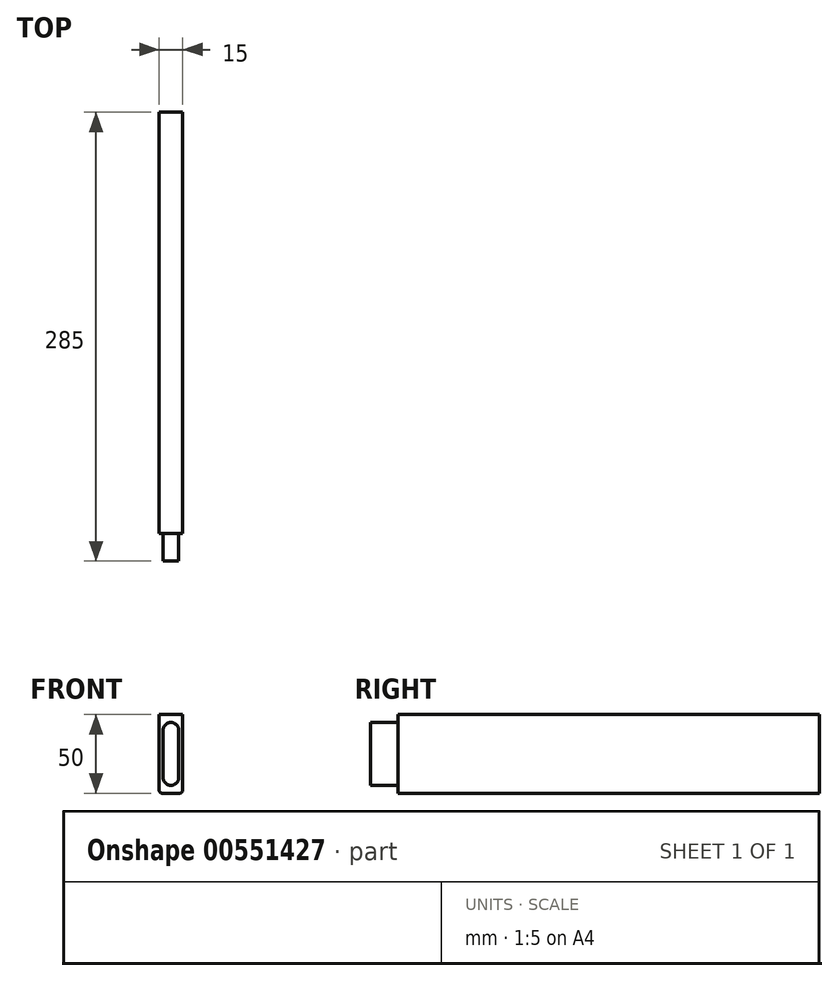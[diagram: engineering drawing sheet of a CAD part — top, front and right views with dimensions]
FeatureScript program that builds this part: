
annotation { "Feature Type Name" : "Feature", "Feature Type Description" : "" }
export const myFeature = defineFeature(function(context is Context, id is Id, definition is map)
    precondition{}
    {
        {
            var Q0;
            Q0=qCreatedBy(makeId("Front.planeOp"),FACE);
            var sketch = newSketch(context, id + "F0", { "sketchPlane" : qUnion([Q0])});
            skLineSegment(sketch, "E0.bottom", {"start": v(-7.5, -25) * mm, "end": v(7.5, -25) * mm});
            skLineSegment(sketch, "E0.top", {"start": v(-7.5, 25) * mm, "end": v(7.5, 25) * mm});
            skLineSegment(sketch, "E0.left", {"start": v(-7.5, -25) * mm, "end": v(-7.5, 25) * mm});
            skLineSegment(sketch, "E0.right", {"start": v(7.5, -25) * mm, "end": v(7.5, 25) * mm});
            skPoint(sketch, "E0.middle", {"position": v(0, 0) * mm});
            skSolve(sketch);
        }
        {
            var Q0;
            Q0 = qSketchRegion(id + "F0", true);
            extrude(context, id + "F1", {"entities" : qUnion([Q0]), "depth" : 142.5 * mm, "offsetDistance" : 25 * mm, "hasSecondDirection" : true, "secondDirectionOppositeDirection" : true, "secondDirectionDepth" : 142.5 * mm});
        }
        {
            var Q0;
            Q0=makeQuery(id+"F1.opExtrude","CAP_FACE",FACE,{"disambiguationData":[OSD([sQuery(id+"F0.wireOp",EDGE,"E0.bottom"),sQuery(id+"F0.wireOp",EDGE,"E0.top"),sQuery(id+"F0.wireOp",EDGE,"E0.left"),sQuery(id+"F0.wireOp",EDGE,"E0.right")])],"isStart":false});
            var sketch = newSketch(context, id + "F2", { "sketchPlane" : qUnion([Q0])});
            skLineSegment(sketch, "E1.bottom", {"start": v(-5, -15) * mm, "end": v(5, -15) * mm});
            skLineSegment(sketch, "E1.top", {"start": v(-5, 15) * mm, "end": v(5, 15) * mm});
            skLineSegment(sketch, "E1.left", {"start": v(-5, -15) * mm, "end": v(-5, 15) * mm});
            skLineSegment(sketch, "E1.right", {"start": v(5, -15) * mm, "end": v(5, 15) * mm});
            skPoint(sketch, "E1.middle", {"position": v(0, 0) * mm});
            skCircle(sketch, "E2", {"center": v(0, 15) * mm, "radius": 5 * mm});
            skCircle(sketch, "E3", {"center": v(0, -15) * mm, "radius": 5 * mm});
            skLineSegment(sketch, "E4.0", {"start": v(-7.5, -25) * mm, "end": v(7.5, -25) * mm});
            skLineSegment(sketch, "E5.0.0", {"start": v(7.5, 25) * mm, "end": v(-7.5, 25) * mm});
            skLineSegment(sketch, "E5.0.1", {"start": v(-7.5, 25) * mm, "end": v(-7.5, -25) * mm});
            skLineSegment(sketch, "E5.0.3", {"start": v(7.5, -25) * mm, "end": v(7.5, 25) * mm});
            skSolve(sketch);
        }
        {
            var Q0;
            {var subQ1=sQuery(id+"F2.wireOp",EDGE,"E1.left");Q0=makeQuery(id+"F2.imprint","IMPRINT",FACE,{"disambiguationData":[TD([[makeQuery(id+"F2.imprint","IMPRINT",EDGE,{"derivedFrom":subQ1}),1.0]])]});}
            extrude(context, id + "F3", {"entities" : qUnion([Q0]), "operationType" : NewBodyOperationType.REMOVE, "oppositeDirection" : true, "depth" : 17.5 * mm, "offsetDistance" : 25 * mm});
        }
        {
            var Q0;
            Q0=makeQuery(id+"F1.opExtrude","SWEPT_EDGE",EDGE,{"disambiguationData":[OSD([sQuery(id+"F0.wireOp",EDGE,"E0.bottom"),sQuery(id+"F0.wireOp",EDGE,"E0.right")])]});
            var Q1;
            Q1=makeQuery(id+"F1.opExtrude","SWEPT_EDGE",EDGE,{"disambiguationData":[OSD([sQuery(id+"F0.wireOp",EDGE,"E0.bottom"),sQuery(id+"F0.wireOp",EDGE,"E0.left")])]});
            fillet(context, id + "F4", {"entities" : qUnion([Q0, Q1]), "radius" : 2 * mm, "tangentPropagation" : true, "allowEdgeOverflow" : false});
        }
    });
